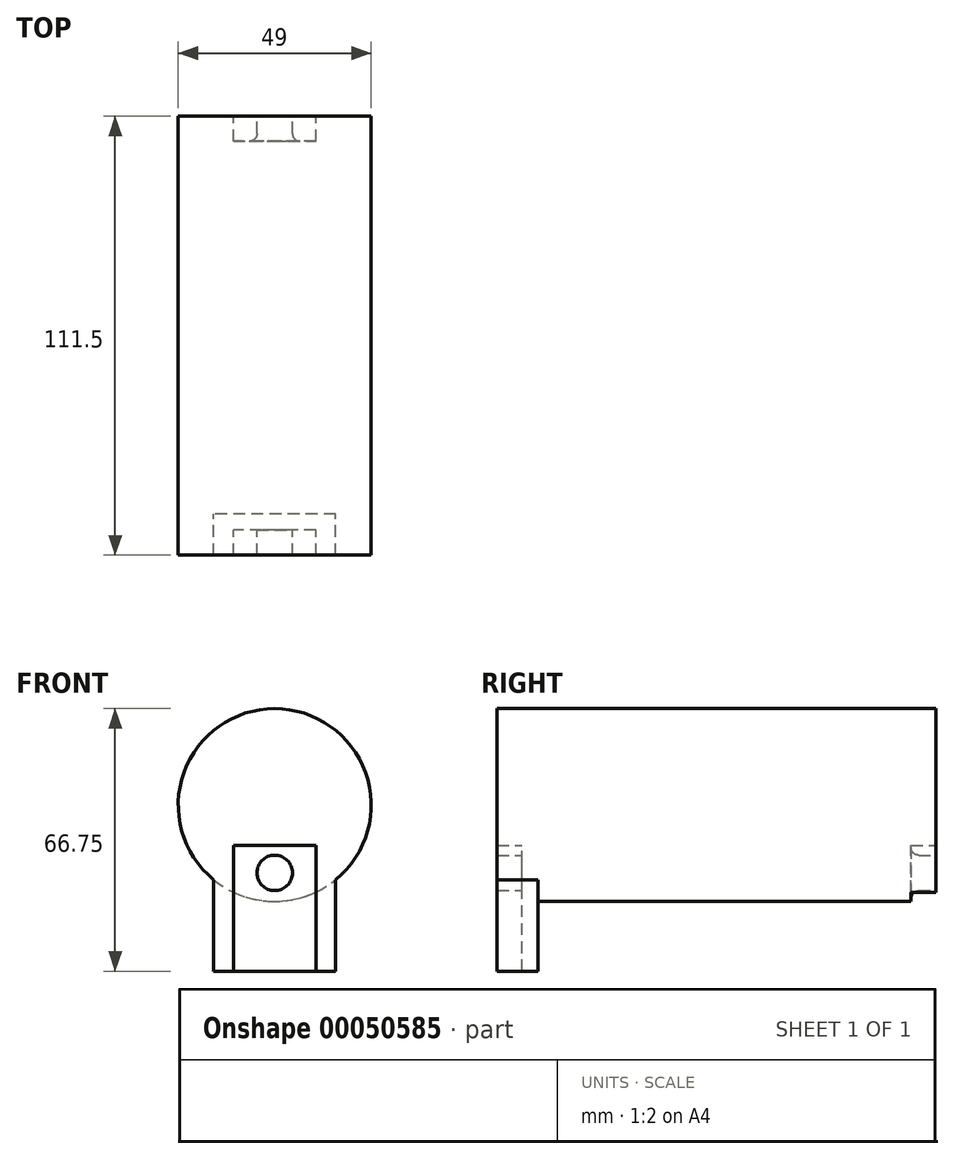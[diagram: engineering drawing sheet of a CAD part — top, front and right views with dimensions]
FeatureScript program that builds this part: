
annotation { "Feature Type Name" : "Feature", "Feature Type Description" : "" }
export const myFeature = defineFeature(function(context is Context, id is Id, definition is map)
    precondition{}
    {
        {
            var Q0;
            Q0=qCreatedBy(makeId("Front.planeOp"),FACE);
            var sketch = newSketch(context, id + "F0", { "sketchPlane" : qUnion([Q0])});
            skCircle(sketch, "E0", {"center": v(0, 17.25) * mm, "radius": 24.5 * mm});
            skSolve(sketch);
        }
        {
            var Q0;
            Q0 = qSketchRegion(id + "F0", true);
            extrude(context, id + "F1", {"entities" : qUnion([Q0]), "depth" : 98.75 * mm, "symmetric" : true});
        }
        {
            var Q0;
            Q0=qCreatedBy(makeId("Front.planeOp"),FACE);
            var sketch = newSketch(context, id + "F2", { "sketchPlane" : qUnion([Q0])});
            skCircle(sketch, "E1", {"center": v(0, 0) * mm, "radius": 4.5 * mm});
            skSolve(sketch);
        }
        {
            var Q0;
            Q0 = qSketchRegion(id + "F2", true);
            extrude(context, id + "F3", {"entities" : qUnion([Q0]), "operationType" : NewBodyOperationType.ADD, "depth" : 111.5 * mm, "symmetric" : true});
        }
        {
            var Q0;
            Q0=qCreatedBy(makeId("Front.planeOp"),FACE);
            var sketch = newSketch(context, id + "F4", { "sketchPlane" : qUnion([Q0])});
            skArc(sketch, "E2.0", {"start": v(10.5, -4.9) * mm, "mid": v(0, 41.75) * mm, "end": v(-10.5, -4.9) * mm});
            skLineSegment(sketch, "E3", {"start": v(-10.5, -4.9) * mm, "end": v(-10.5, 7) * mm});
            skLineSegment(sketch, "E4", {"start": v(-10.5, 7) * mm, "end": v(10.5, 7) * mm});
            skLineSegment(sketch, "E5", {"start": v(10.5, 7) * mm, "end": v(10.5, -4.9) * mm});
            skLineSegment(sketch, "E6", {"start": v(0, 17.25) * mm, "end": v(0, -10.8) * mm, "construction": true});
            skPoint(sketch, "E6.endSnap0", {"position": v(0, 7) * mm});
            skSolve(sketch);
        }
        {
            var Q0;
            Q0 = qSketchRegion(id + "F4", true);
            extrude(context, id + "F5", {"entities" : qUnion([Q0]), "operationType" : NewBodyOperationType.ADD, "depth" : 111.5 * mm, "symmetric" : true});
        }
        {
            var Q0;
            Q0=qCreatedBy(makeId("Top.planeOp"),FACE);
            var sketch = newSketch(context, id + "F6", { "sketchPlane" : qUnion([Q0])});
            skLineSegment(sketch, "E7.0", {"start": v(0, -49.38) * mm, "end": v(-10.5, -49.38) * mm});
            skLineSegment(sketch, "E8.0", {"start": v(-10.5, -55.75) * mm, "end": v(-10.5, -49.38) * mm});
            skLineSegment(sketch, "E9", {"start": v(-10.5, -55.75) * mm, "end": v(-15.5, -55.75) * mm});
            skLineSegment(sketch, "E10", {"start": v(-15.5, -55.75) * mm, "end": v(-15.5, -45.38) * mm});
            skLineSegment(sketch, "E11", {"start": v(-15.5, -45.38) * mm, "end": v(0, -45.38) * mm});
            skLineSegment(sketch, "E12", {"start": v(0, 0) * mm, "end": v(0, -66.08) * mm, "construction": true});
            skPoint(sketch, "E12.endSnap0", {"position": v(0, -49.38) * mm});
            skPoint(sketch, "E13.0.end.orphan", {"position": v(10.5, -49.38) * mm});
            skPoint(sketch, "E13.0.start.orphan", {"position": v(10.5, -55.75) * mm});
            skLineSegment(sketch, "E14.MirrorCS", {"start": v(10.5, -55.75) * mm, "end": v(10.5, -49.38) * mm});
            skLineSegment(sketch, "E15.MirrorCS", {"start": v(0, -49.38) * mm, "end": v(10.5, -49.38) * mm});
            skLineSegment(sketch, "E16.MirrorCS", {"start": v(15.5, -45.38) * mm, "end": v(0, -45.38) * mm});
            skLineSegment(sketch, "E17.MirrorCS", {"start": v(15.5, -55.75) * mm, "end": v(15.5, -45.38) * mm});
            skLineSegment(sketch, "E18.MirrorCS", {"start": v(10.5, -55.75) * mm, "end": v(15.5, -55.75) * mm});
            skSolve(sketch);
        }
        {
            var Q0;
            Q0 = qSketchRegion(id + "F6", true);
            extrude(context, id + "F7", {"entities" : qUnion([Q0]), "operationType" : NewBodyOperationType.ADD, "oppositeDirection" : true, "depth" : 25 * mm});
        }
        {
            var Q0;
            Q0=makeQuery(id+"F3.boolean.opBoolean","INTERSECT",EDGE,{"derivedFrom":[makeQuery(id+"F1.opExtrude","CAP_FACE",FACE,{"disambiguationData":[OSD([sQuery(id+"F0.wireOp",EDGE,"E0")])],"isStart":true}),makeQuery(id+"F3.opExtrude","SWEPT_FACE",FACE,{"disambiguationData":[OSD([sQuery(id+"F2.wireOp",EDGE,"E1")])]})]});
            var Q1;
            Q1=makeQuery(id+"F3.boolean.opBoolean","INTERSECT",EDGE,{"derivedFrom":[makeQuery(id+"F1.opExtrude","CAP_FACE",FACE,{"disambiguationData":[OSD([sQuery(id+"F0.wireOp",EDGE,"E0")])],"isStart":false}),makeQuery(id+"F3.opExtrude","SWEPT_FACE",FACE,{"disambiguationData":[OSD([sQuery(id+"F2.wireOp",EDGE,"E1")])]})]});
            fillet(context, id + "F8", {"entities" : qUnion([Q0, Q1]), "radius" : 2 * mm, "tangentPropagation" : true, "allowEdgeOverflow" : false});
        }
    });
